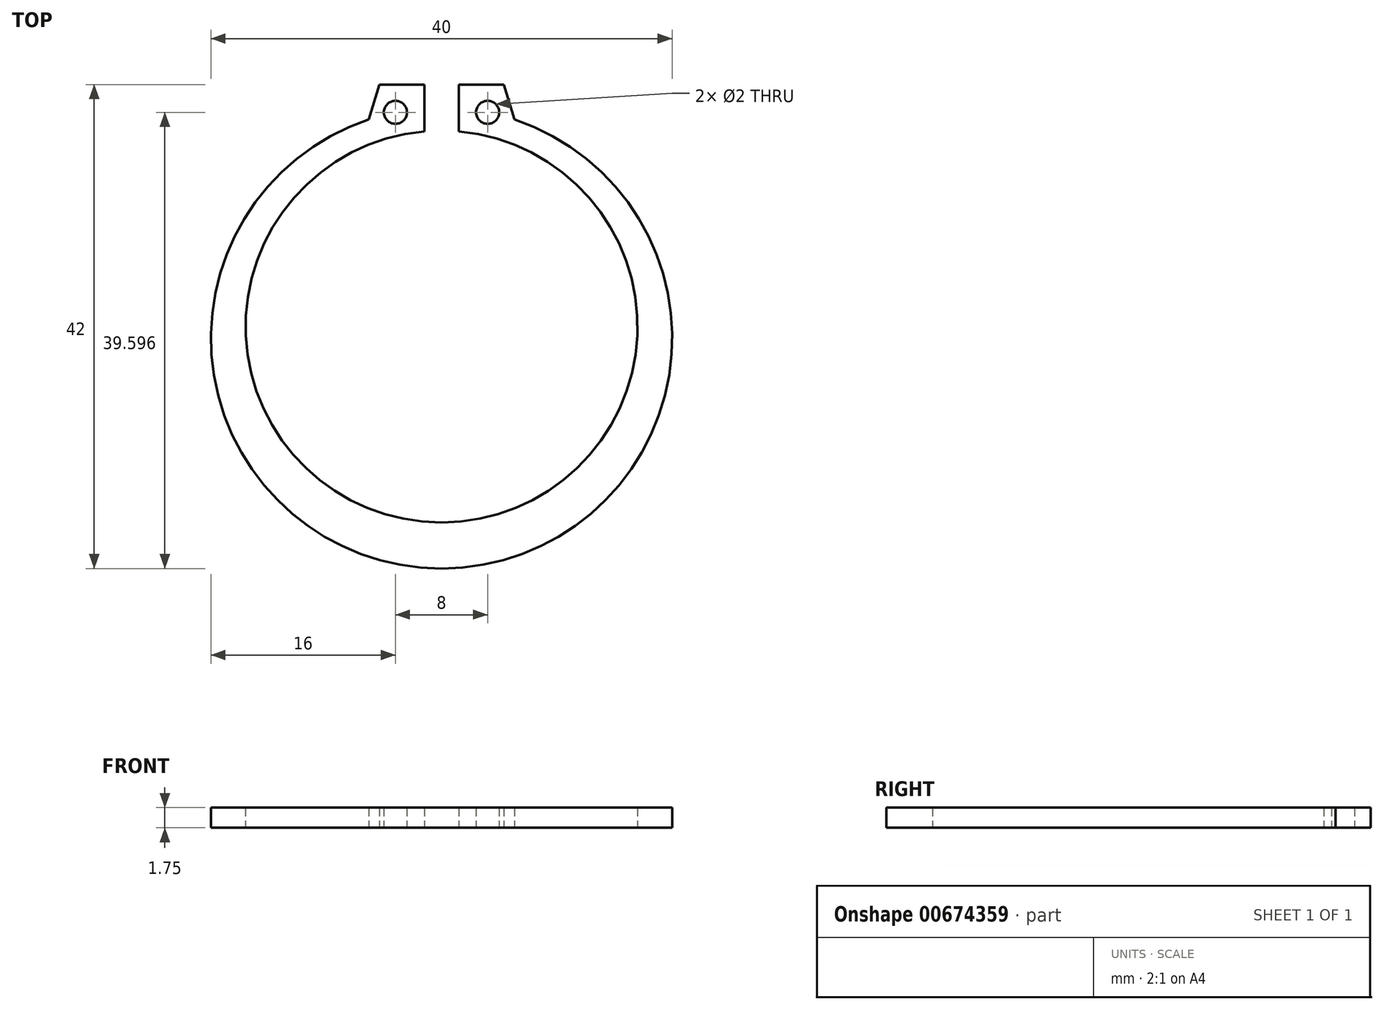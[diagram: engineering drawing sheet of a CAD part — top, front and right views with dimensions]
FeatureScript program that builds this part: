
annotation { "Feature Type Name" : "Feature", "Feature Type Description" : "" }
export const myFeature = defineFeature(function(context is Context, id is Id, definition is map)
    precondition{}
    {
        {
            var Q0;
            Q0=qCreatedBy(makeId("Top.planeOp"),FACE);
            var sketch = newSketch(context, id + "F0", { "sketchPlane" : qUnion([Q0])});
            skArc(sketch, "E0", {"start": v(-6.33, 18.97) * mm, "mid": v(-19.74, -3.2) * mm, "end": v(0, -20) * mm});
            skLineSegment(sketch, "E1", {"start": v(0, 0) * mm, "end": v(0, 1) * mm, "construction": true});
            skArc(sketch, "E2", {"start": v(-1.5, 17.93) * mm, "mid": v(-16.98, 0.25) * mm, "end": v(0, -16) * mm});
            skLineSegment(sketch, "E3", {"start": v(0, 0) * mm, "end": v(0, 18) * mm, "construction": true});
            skLineSegment(sketch, "E4", {"start": v(0, 28.86) * mm, "end": v(-1.5, 28.86) * mm, "construction": true});
            skLineSegment(sketch, "E5", {"start": v(-1.5, 28.86) * mm, "end": v(-1.5, 19.94) * mm});
            skLineSegment(sketch, "E6", {"start": v(0, 20) * mm, "end": v(0, 22) * mm, "construction": true});
            skLineSegment(sketch, "E7", {"start": v(-1.5, 22) * mm, "end": v(-5.4, 22) * mm});
            skLineSegment(sketch, "E8", {"start": v(-5.4, 22) * mm, "end": v(-6.33, 18.97) * mm});
            skLineSegment(sketch, "E9", {"start": v(0, 28.86) * mm, "end": v(-4, 28.86) * mm, "construction": true});
            skLineSegment(sketch, "E10", {"start": v(-4, 28.86) * mm, "end": v(-4, 14) * mm, "construction": true});
            skPoint(sketch, "E11", {"position": v(-4, 19.6) * mm});
            skCircle(sketch, "E12", {"center": v(-4, 19.6) * mm, "radius": 1 * mm});
            skPoint(sketch, "E13.trimOffspring.end.orphan", {"position": v(-1.5, 0) * mm});
            skLineSegment(sketch, "E14", {"start": v(-1.5, 19.94) * mm, "end": v(-1.5, 17.93) * mm});
            skLineSegment(sketch, "E15", {"start": v(0, 32.7) * mm, "end": v(0, -22.48) * mm});
            skLineSegment(sketch, "E16.trimOffspring", {"start": v(0, 20) * mm, "end": v(0, 28.86) * mm, "construction": true});
            skSolve(sketch);
        }
        {
            var Q0;
            {var subQ4=sQuery(id+"F0.wireOp",EDGE,"E0");Q0=makeQuery(id+"F0.imprint","IMPRINT",FACE,{"disambiguationData":[TD([[makeQuery(id+"F0.imprint","IMPRINT",EDGE,{"derivedFrom":subQ4}),1.0]])]});}
            extrude(context, id + "F1", {"entities" : qUnion([Q0]), "depth" : 1.75 * mm, "offsetDistance" : 25 * mm});
        }
        {
            var Q0;
            Q0=makeQuery(id+"F1.opExtrude","SWEPT_BODY",BODY,{"disambiguationData":[OSD([sQuery(id+"F0.wireOp",EDGE,"E0"),sQuery(id+"F0.wireOp",EDGE,"E2"),sQuery(id+"F0.wireOp",EDGE,"E5"),sQuery(id+"F0.wireOp",EDGE,"E7"),sQuery(id+"F0.wireOp",EDGE,"E8"),sQuery(id+"F0.wireOp",EDGE,"E12"),sQuery(id+"F0.wireOp",EDGE,"E14"),sQuery(id+"F0.wireOp",EDGE,"E15")])]});
            var Q1;
            Q1=qCreatedBy(makeId("Right.planeOp"),FACE);
            mirror(context, id + "F2", {"operationType" : NewBodyOperationType.ADD, "entities" : qUnion([Q0]), "mirrorPlane" : qUnion([Q1])});
        }
    });
